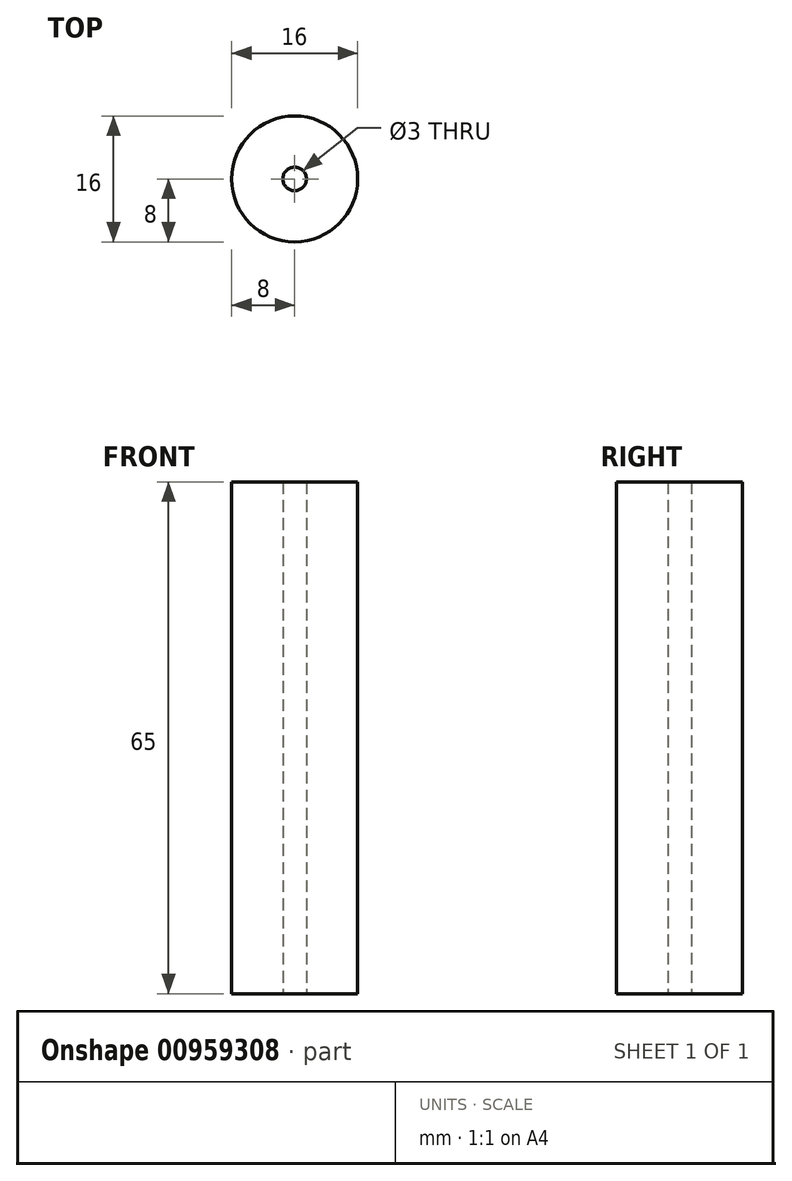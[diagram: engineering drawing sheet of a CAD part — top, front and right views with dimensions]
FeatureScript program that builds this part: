
annotation { "Feature Type Name" : "Feature", "Feature Type Description" : "" }
export const myFeature = defineFeature(function(context is Context, id is Id, definition is map)
    precondition{}
    {
        {
            var Q0;
            Q0=qCreatedBy(makeId("Top.planeOp"),FACE);
            var sketch = newSketch(context, id + "F0", { "sketchPlane" : qUnion([Q0])});
            skCircle(sketch, "E0", {"center": v(0, 0) * mm, "radius": 1.5 * mm});
            skCircle(sketch, "E1", {"center": v(0, 0) * mm, "radius": 8 * mm});
            skSolve(sketch);
        }
        {
            var Q0;
            Q0 = qSketchRegion(id + "F0", true);
            extrude(context, id + "F1", {"entities" : qUnion([Q0]), "depth" : 65 * mm, "offsetDistance" : 25.4 * mm});
        }
    });
